# Revit family: 603-A-6100-DN250
name_source: partatom
category: Pipe Accessories
units: mm (PartAtom-declared; Revit-internal decimal feet)

## family parameters
Always vertical = Yes
Cut with Voids When Loaded = No
Part Type = Valve - Breaks Into
Round Connector Dimension = Use Diameter
Shared = No
Work Plane-Based = No

## types (3) — shared parameters
Bolt_width = 20 mm  [stored 0.0656168 ft]
Bottm_cut = 160 mm  [stored 0.524934 ft]
Bottm_height = 7 mm  [stored 0.0229659 ft]
Bottom_Flange_Thicckness = 12 mm  [stored 0.0393701 ft]
D = 203 mm  [stored 0.66601 ft]
D3 = 167 mm
D4 = 187 mm  [stored 0.613517 ft]
DN250_242 - 268 = 603-268-000-6100
DN250_266 - 292 = 603-292-000-6100
DN250_280 - 306 = 603-306-000-6100
Description_ = AVK UNIVERSAL SUPA® FLANGE ADAPTOR
H1 = 35 mm  [stored 0.114829 ft]
ID = 125 mm  [stored 0.410105 ft]
L = 112 mm  [stored 0.367454 ft]
L1 = 58 mm  [stored 0.190289 ft]
Nomianal_Diameter(DN) = 250 mm  [stored 0.82021 ft]
Nut = 10 mm  [stored 0.0328084 ft]
PCD = 350 mm  [stored 1.14829 ft]
Rib_Thickness = 5 mm  [stored 0.0164042 ft]
Rib_length = 32 mm  [stored 0.104987 ft]
Rib_width = 410 mm  [stored 1.34514 ft]
Search_table = 603-A-6100-DN250
URL product pages = https://www.avkvalves.com
Washer = 3 mm  [stored 0.00984252 ft]

## per-type parameters (varying)
| type | Bolt_Ref | Bottm_height_2 | D2 | DN1 | DN1_ref | DN2 | DN2_ref | Max_Height | Washer_Ref |
| DN250_266 - 292 | 25 mm  [stored 0.082021 ft] | 10 mm  [stored 0.0328084 ft] | 155 mm  [stored 0.50853 ft] | 146 mm  [stored 0.479003 ft] | 292 mm  [stored 0.958005 ft] | 133 mm  [stored 0.436352 ft] | 266 mm  [stored 0.872703 ft] | 180 mm  [stored 0.590551 ft] | 35 mm  [stored 0.114829 ft] |
| DN250_280 - 306 | 25 mm  [stored 0.082021 ft] | 10 mm  [stored 0.0328084 ft] | 160 mm  [stored 0.524934 ft] | 153 mm  [stored 0.501969 ft] | 306 mm  [stored 1.00394 ft] | 140 mm  [stored 0.459318 ft] | 280 mm  [stored 0.918635 ft] | 180 mm  [stored 0.590551 ft] | 35 mm  [stored 0.114829 ft] |
| DN250_242 - 268 | 20 mm  [stored 0.0656168 ft] | 5 mm  [stored 0.0164042 ft] | 145 mm  [stored 0.475722 ft] | 134 mm | 268 mm  [stored 0.879265 ft] | 121 mm  [stored 0.396982 ft] | 242 mm  [stored 0.793963 ft] | 175 mm  [stored 0.574147 ft] | 30 mm  [stored 0.0984252 ft] |

note: [stored X ft] marks values corroborated as IEEE doubles in the binary element streams (Revit-internal decimal feet)

## geometry (parser evidence)
native form markers: Sweep x8
no freeform markers — native parametric forms only
